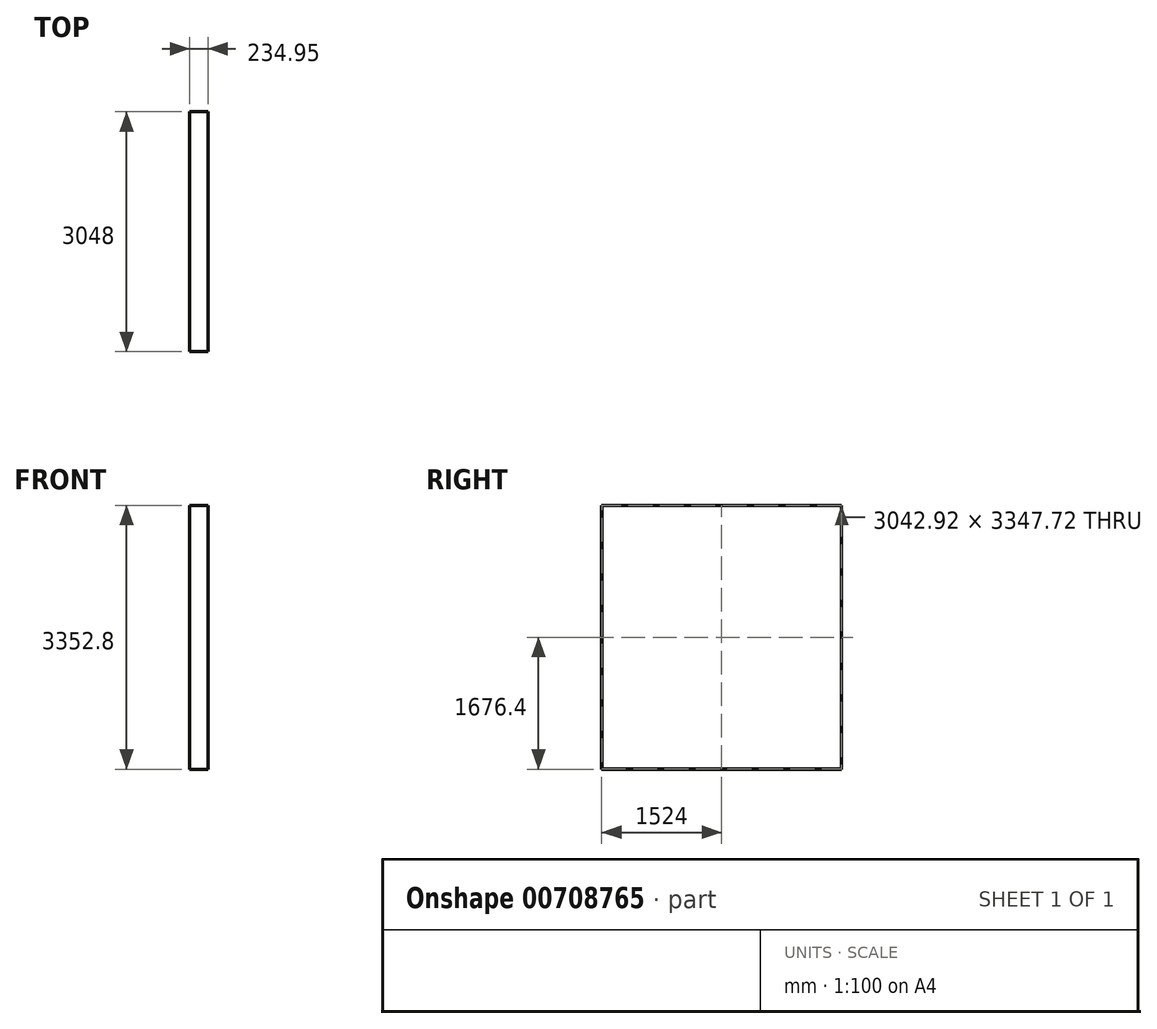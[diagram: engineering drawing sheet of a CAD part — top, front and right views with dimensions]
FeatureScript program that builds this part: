
annotation { "Feature Type Name" : "Feature", "Feature Type Description" : "" }
export const myFeature = defineFeature(function(context is Context, id is Id, definition is map)
    precondition{}
    {
        {
            var Q0;
            Q0=qCreatedBy(makeId("Front.planeOp"),FACE);
            var sketch = newSketch(context, id + "F0", { "sketchPlane" : qUnion([Q0])});
            skLineSegment(sketch, "E0", {"start": v(0, 0) * mm, "end": v(234.95, 0) * mm});
            skLineSegment(sketch, "E1", {"start": v(234.95, 0) * mm, "end": v(234.95, 3352.8) * mm});
            skLineSegment(sketch, "E2", {"start": v(234.95, 3352.8) * mm, "end": v(0, 3352.8) * mm});
            skLineSegment(sketch, "E3", {"start": v(0, 3352.8) * mm, "end": v(0, 0) * mm});
            skSolve(sketch);
        }
        {
            var Q0;
            Q0 = qSketchRegion(id + "F0", true);
            extrude(context, id + "F1", {"entities" : qUnion([Q0]), "depth" : 3048 * mm, "offsetDistance" : 25.4 * mm});
        }
        {
            var Q0;
            Q0=makeQuery(id+"F1.opExtrude","SWEPT_FACE",FACE,{"disambiguationData":[OSD([sQuery(id+"F0.wireOp",EDGE,"E1")])]});
            var sketch = newSketch(context, id + "F2", { "sketchPlane" : qUnion([Q0])});
            skLineSegment(sketch, "E4.bottom", {"start": v(-3045.46, 2.54) * mm, "end": v(-2.54, 2.54) * mm});
            skLineSegment(sketch, "E4.top", {"start": v(-3045.46, 3350.26) * mm, "end": v(-2.54, 3350.26) * mm});
            skLineSegment(sketch, "E4.left", {"start": v(-3045.46, 2.54) * mm, "end": v(-3045.46, 3350.26) * mm});
            skLineSegment(sketch, "E4.right", {"start": v(-2.54, 2.54) * mm, "end": v(-2.54, 3350.26) * mm});
            skSolve(sketch);
        }
        {
            var Q0;
            Q0=makeQuery(id+"F2.imprint","IMPRINT",FACE,{"disambiguationData":[TD([[makeQuery(id+"F2.imprint","IMPRINT",EDGE,{"derivedFrom":sQuery(id+"F2.wireOp",EDGE,"E4.bottom")}),1.0]])]});
            extrude(context, id + "F3", {"entities" : qUnion([Q0]), "operationType" : NewBodyOperationType.REMOVE, "endBound" : BoundingType.UP_TO_NEXT, "oppositeDirection" : true, "depth" : 25.4 * mm, "offsetDistance" : 25.4 * mm});
        }
    });
